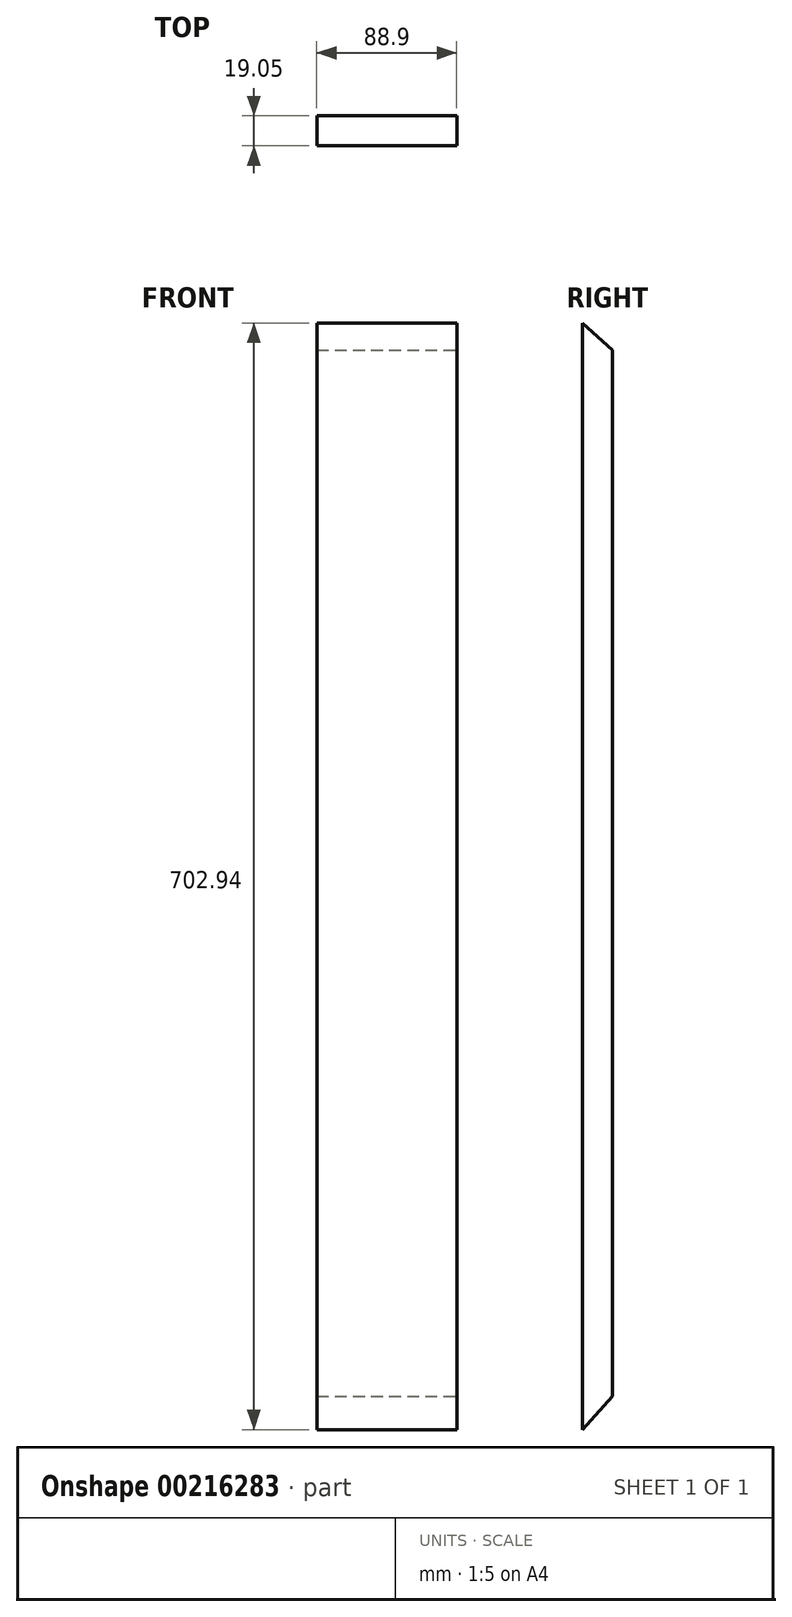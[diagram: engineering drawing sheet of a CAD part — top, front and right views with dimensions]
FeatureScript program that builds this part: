
annotation { "Feature Type Name" : "Feature", "Feature Type Description" : "" }
export const myFeature = defineFeature(function(context is Context, id is Id, definition is map)
    precondition{}
    {
        {
            var Q0;
            Q0=qCreatedBy(makeId("Front.planeOp"),FACE);
            var sketch = newSketch(context, id + "F0", { "sketchPlane" : qUnion([Q0])});
            skLineSegment(sketch, "E0", {"start": v(2185.66, 2882.9) * mm, "end": v(2274.56, 2882.9) * mm});
            skLineSegment(sketch, "E1", {"start": v(2274.56, 2882.9) * mm, "end": v(2274.56, 2179.64) * mm});
            skLineSegment(sketch, "E2", {"start": v(2274.56, 2179.96) * mm, "end": v(2185.66, 2179.96) * mm});
            skLineSegment(sketch, "E3", {"start": v(2185.66, 2179.96) * mm, "end": v(2185.66, 2883.22) * mm});
            skSolve(sketch);
        }
        {
            var Q0;
            {var subQ0=sQuery(id+"F0.wireOp",EDGE,"E0");Q0=makeQuery(id+"F0.imprint","IMPRINT",FACE,{"disambiguationData":[TD([[makeQuery(id+"F0.imprint","IMPRINT",EDGE,{"derivedFrom":subQ0}),-1.0]])]});}
            extrude(context, id + "F1", {"entities" : qUnion([Q0]), "depth" : 19.05 * mm});
        }
        {
            var Q0;
            Q0=makeQuery(id+"F1.opExtrude","SWEPT_FACE",FACE,{"disambiguationData":[OSD([sQuery(id+"F0.wireOp",EDGE,"E1")])]});
            var sketch = newSketch(context, id + "F2", { "sketchPlane" : qUnion([Q0])});
            skLineSegment(sketch, "E4", {"start": v(-19.05, 2882.9) * mm, "end": v(0, 2882.9) * mm});
            skLineSegment(sketch, "E5", {"start": v(0, 2882.9) * mm, "end": v(0, 2865.8) * mm});
            skLineSegment(sketch, "E6", {"start": v(0, 2865.8) * mm, "end": v(-19.05, 2882.9) * mm});
            skLineSegment(sketch, "E7", {"start": v(-19.05, 2179.96) * mm, "end": v(0, 2179.96) * mm});
            skLineSegment(sketch, "E8", {"start": v(0, 2179.96) * mm, "end": v(0, 2201.16) * mm});
            skLineSegment(sketch, "E9", {"start": v(0, 2201.16) * mm, "end": v(-19.05, 2179.96) * mm});
            skSolve(sketch);
        }
        {
            var Q0;
            Q0=makeQuery(id+"F2.imprint","IMPRINT",FACE,{"disambiguationData":[TD([[makeQuery(id+"F2.imprint","IMPRINT",EDGE,{"derivedFrom":sQuery(id+"F2.wireOp",EDGE,"E7")}),1.0]])]});
            extrude(context, id + "F3", {"entities" : qUnion([Q0]), "operationType" : NewBodyOperationType.REMOVE, "endBound" : BoundingType.THROUGH_ALL, "oppositeDirection" : true, "depth" : 25.4 * mm});
        }
        {
            var Q0;
            Q0=makeQuery(id+"F2.imprint","IMPRINT",FACE,{"disambiguationData":[TD([[makeQuery(id+"F2.imprint","IMPRINT",EDGE,{"derivedFrom":sQuery(id+"F2.wireOp",EDGE,"E4")}),-1.0]])]});
            extrude(context, id + "F4", {"entities" : qUnion([Q0]), "operationType" : NewBodyOperationType.REMOVE, "endBound" : BoundingType.THROUGH_ALL, "oppositeDirection" : true, "depth" : 25.4 * mm});
        }
    });
